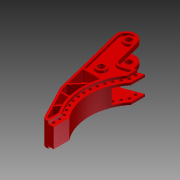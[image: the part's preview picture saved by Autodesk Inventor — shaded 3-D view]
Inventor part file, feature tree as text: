
AUTODESK INVENTOR PART (.ipt)
format: ipt  version: 2013 (Build 170138000, 138)  size: 428,032 bytes
history: native  units: in
note: dims shown in document units (in); Inventor stores cm internally (conversion verified against a paired STEP export)
features: extrude x6, sketch x6, mirror x2, hole x2, plane x1, fillet x1, pattern_linear x1, projected_geometry x1
ambient origin geometry x8: Origin, YZ Plane, XZ Plane, XY Plane, X Axis, Y Axis, Z Axis, Center Point
bodies: Solid1 (feature_tree)
feature tree (20):
  extrude  "Extrusion1"  Depth=0.9958in
  sketch  "Sketch2"  dims[d2=0.4152in d3=0.5696in]
  extrude  "Extrusion2"  Depth=0.5696in
  extrude  "Extrusion3"  Depth=0.5289in
  plane  "Work Plane1"
  mirror  "Mirror1"
  sketch  "Sketch3"  dims[d4=0.25in d5=0.5289in]
  extrude  "Extrusion4"  Depth=0.125in
  extrude  "Extrusion5"  Depth=1.4969in
  mirror  "Mirror2"
  extrude  "Extrusion6"  Depth=0.125in
  fillet  "Fillet1"  Radius=0.125in
  hole  "Hole1"  [1 undecoded]
  sketch  "Sketch6"  dims[d10=0.276in d11=0.125in d12=0.125in d13=0.645in d14=0.0in d15=0.3in d16=0.0in d17=0.066in d18=0.0in d21=0.152in d22=0.152in d23=0.559in d24=0.0in d25=0.063in d26=0.0in d27=0.4in d28=0.0in d29=0.165in d30=0.75in d31=0.375in d32=0.25in d33=0.5635in d34=1.0in d35=0.8108in d36=0.284in d37=0.039in d38=0.098in d39=0.078in d40=0.75in d41=0.375in d42=0.25in d43=0.5635in d44=1.0in d45=0.8108in d46=0.098in d47=5.9055in d49=0.039in d50=0.039in]
  hole  "Hole2"  [1 undecoded]
  pattern_linear  "Rectangular Pattern1"  Spacing1=0.066in  [1 undecoded]
  sketch  "Sketch1"  dims[d0=0.8792in d1=0.9958in]
  projected_geometry  "Projected Loop1"
  sketch  "Sketch4"  dims[d6=0.0522in d7=0.125in]
  sketch  "Sketch5"  dims[d8=0.3665in d9=1.4969in]
note: 3 required parameter values undecoded (feature->parameter linkage not recoverable at this tier; creation-order binding heuristic only, values carry confidence <= 0.55)
